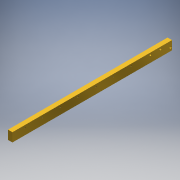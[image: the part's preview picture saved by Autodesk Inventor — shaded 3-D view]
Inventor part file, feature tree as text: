
AUTODESK INVENTOR PART (.ipt)
format: ipt  version: 2017 (Build 210142000, 142)  size: 155,648 bytes
history: native  units: in
note: dims shown in document units (in); Inventor stores cm internally (conversion verified against a paired STEP export)
features: hole x4, pattern_linear x4, sketch x3, extrude x1
ambient origin geometry x8: Origin, YZ Plane, XZ Plane, XY Plane, X Axis, Y Axis, Z Axis, Center Point
bodies: Solid1 (feature_tree)
feature tree (12):
  extrude  "Extrusion1"  Depth=0.5in
  sketch  "Sketch3"  dims[d6=9.0in d7=0.0in d8=0.1344in]
  hole  "Hole1"  [1 undecoded]
  pattern_linear  "Rectangular Pattern1"  Count1=7 Spacing1=1.0in
  sketch  "Sketch6"  dims[d9=0.7in d10=0.067in d11=0.75in d12=0.375in d13=0.25in d14=0.5635in d15=1.0in d16=0.8108in d17=2.7559in d19=1.0in d20=0.75in d23=0.8108in d24=0.5635in d25=0.25in d26=0.375in d27=0.25in d28=0.067in d45=7.793in d46=0.121in d47=0.109in d48=0.75in d49=0.375in d50=0.25in d51=0.5635in d52=0.26in d53=0.8108in d54=1.1811in d56=0.561in d57=0.7874in d59=0.197in d61=0.067in d62=0.75in d63=0.375in d64=0.25in d65=0.5635in d66=0.25in d67=0.8108in d68=2.3in d69=0.15in d70=0.7874in d72=1.0in d73=1.9685in d75=1.5in d76=0.125in d77=0.125in]
  hole  "Hole4"  [1 undecoded]
  pattern_linear  "Rectangular Pattern4"  Spacing1=7.793in  [1 undecoded]
  hole  "Hole5"  [1 undecoded]
  pattern_linear  "Rectangular Pattern5"  Count1=3 Spacing1=0.561in
  pattern_linear  "Rectangular Pattern6"  Spacing1=2.3in  [1 undecoded]
  sketch  "Sketch2"  dims[d3=0.25in d5=0.5in]
  hole  "Hole2"  [1 undecoded]
note: 6 required parameter values undecoded (feature->parameter linkage not recoverable at this tier; creation-order binding heuristic only, values carry confidence <= 0.55)
